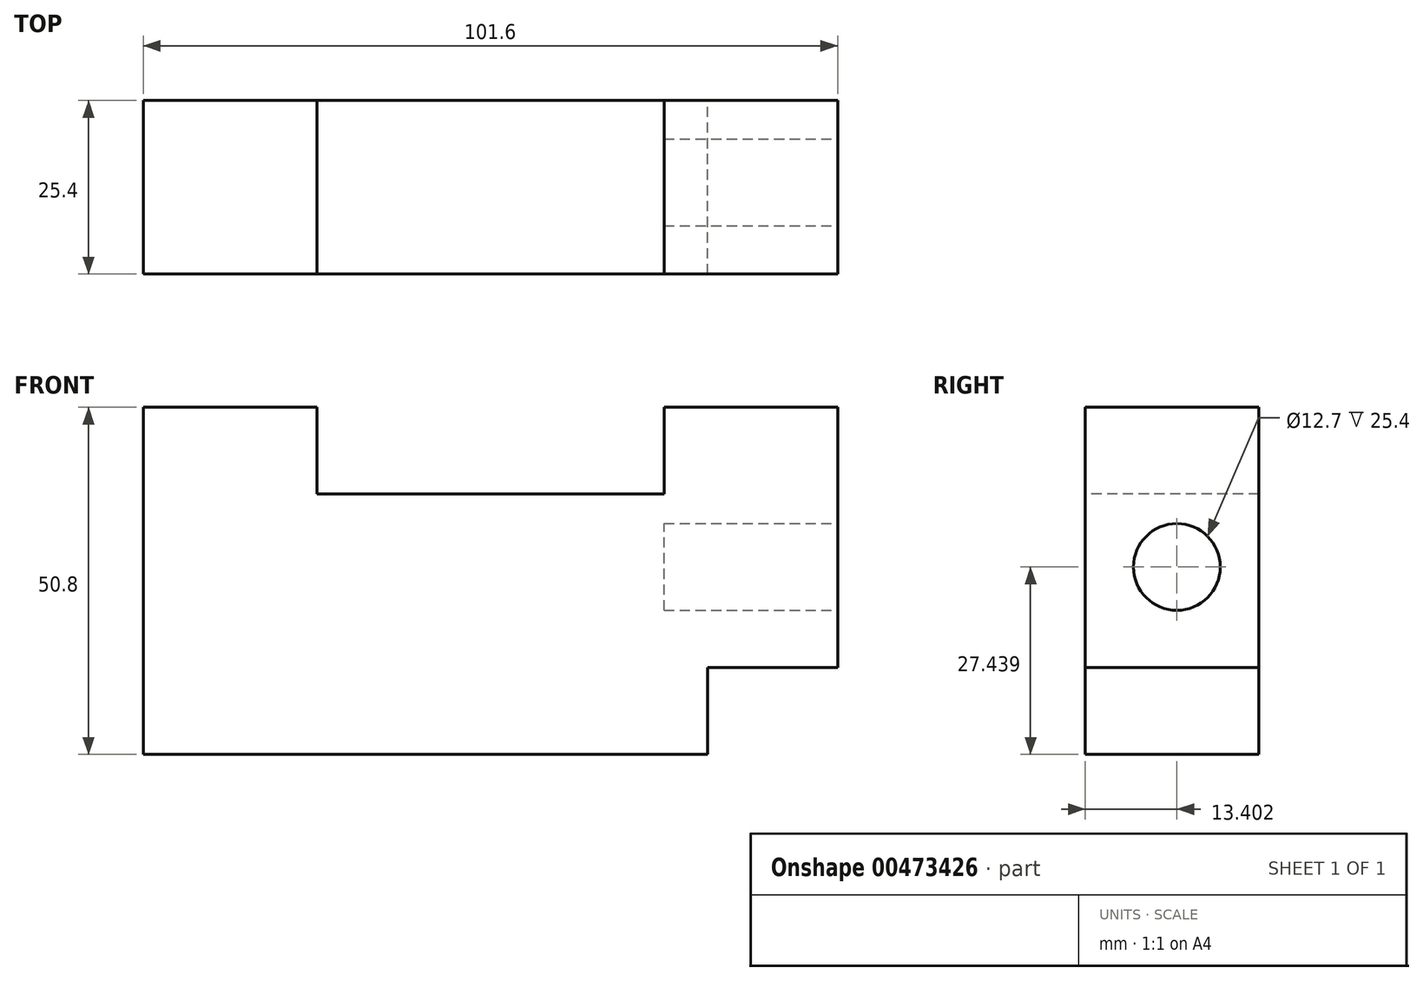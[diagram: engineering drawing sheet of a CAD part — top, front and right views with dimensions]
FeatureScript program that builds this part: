
annotation { "Feature Type Name" : "Feature", "Feature Type Description" : "" }
export const myFeature = defineFeature(function(context is Context, id is Id, definition is map)
    precondition{}
    {
        {
            var Q0;
            Q0=qCreatedBy(makeId("Front.planeOp"),FACE);
            var sketch = newSketch(context, id + "F0", { "sketchPlane" : qUnion([Q0])});
            skLineSegment(sketch, "E0.bottom", {"start": v(-50.8, 25.4) * mm, "end": v(50.8, 25.4) * mm});
            skLineSegment(sketch, "E0.top", {"start": v(-50.8, -25.4) * mm, "end": v(50.8, -25.4) * mm});
            skLineSegment(sketch, "E0.left", {"start": v(-50.8, 25.4) * mm, "end": v(-50.8, -25.4) * mm});
            skLineSegment(sketch, "E0.right", {"start": v(50.8, 25.4) * mm, "end": v(50.8, -25.4) * mm});
            skPoint(sketch, "E0.middle", {"position": v(0, 0) * mm});
            skSolve(sketch);
        }
        {
            var Q0;
            Q0 = qSketchRegion(id + "F0", true);
            extrude(context, id + "F1", {"entities" : qUnion([Q0]), "depth" : 25.4 * mm});
        }
        {
            var Q0;
            Q0=makeQuery(id+"F1.opExtrude","CAP_FACE",FACE,{"disambiguationData":[OSD([sQuery(id+"F0.wireOp",EDGE,"E0.bottom"),sQuery(id+"F0.wireOp",EDGE,"E0.top"),sQuery(id+"F0.wireOp",EDGE,"E0.left"),sQuery(id+"F0.wireOp",EDGE,"E0.right")])],"isStart":false});
            var sketch = newSketch(context, id + "F2", { "sketchPlane" : qUnion([Q0])});
            skLineSegment(sketch, "E1.bottom", {"start": v(-25.4, 25.4) * mm, "end": v(25.4, 25.4) * mm});
            skLineSegment(sketch, "E1.top", {"start": v(-25.4, 12.7) * mm, "end": v(25.4, 12.7) * mm});
            skLineSegment(sketch, "E1.left", {"start": v(-25.4, 25.4) * mm, "end": v(-25.4, 12.7) * mm});
            skLineSegment(sketch, "E1.right", {"start": v(25.4, 25.4) * mm, "end": v(25.4, 12.7) * mm});
            skSolve(sketch);
        }
        {
            var Q0;
            Q0 = qSketchRegion(id + "F2", true);
            extrude(context, id + "F3", {"entities" : qUnion([Q0]), "operationType" : NewBodyOperationType.REMOVE, "endBound" : BoundingType.THROUGH_ALL, "oppositeDirection" : true, "depth" : 25.4 * mm});
        }
        {
            var Q0;
            Q0=makeQuery(id+"F1.opExtrude","SWEPT_FACE",FACE,{"disambiguationData":[OSD([sQuery(id+"F0.wireOp",EDGE,"E0.right")])]});
            var sketch = newSketch(context, id + "F4", { "sketchPlane" : qUnion([Q0])});
            skLineSegment(sketch, "E2.bottom", {"start": v(-25.4, -25.4) * mm, "end": v(0, -25.4) * mm});
            skLineSegment(sketch, "E2.top", {"start": v(-25.4, -12.7) * mm, "end": v(0, -12.7) * mm});
            skLineSegment(sketch, "E2.left", {"start": v(-25.4, -25.4) * mm, "end": v(-25.4, -12.7) * mm});
            skLineSegment(sketch, "E2.right", {"start": v(0, -25.4) * mm, "end": v(0, -12.7) * mm});
            skSolve(sketch);
        }
        {
            var Q0;
            Q0 = qSketchRegion(id + "F4", true);
            extrude(context, id + "F5", {"entities" : qUnion([Q0]), "operationType" : NewBodyOperationType.REMOVE, "oppositeDirection" : true, "depth" : 19.05 * mm});
        }
        {
            var Q0;
            Q0=makeQuery(id+"F1.opExtrude","SWEPT_FACE",FACE,{"disambiguationData":[OSD([sQuery(id+"F0.wireOp",EDGE,"E0.right")])]});
            var sketch = newSketch(context, id + "F6", { "sketchPlane" : qUnion([Q0])});
            skCircle(sketch, "E3", {"center": v(-12, 2.04) * mm, "radius": 6.35 * mm});
            skSolve(sketch);
        }
        {
            var Q0;
            Q0 = qSketchRegion(id + "F6", true);
            extrude(context, id + "F7", {"entities" : qUnion([Q0]), "operationType" : NewBodyOperationType.REMOVE, "oppositeDirection" : true, "depth" : 25.4 * mm});
        }
    });
